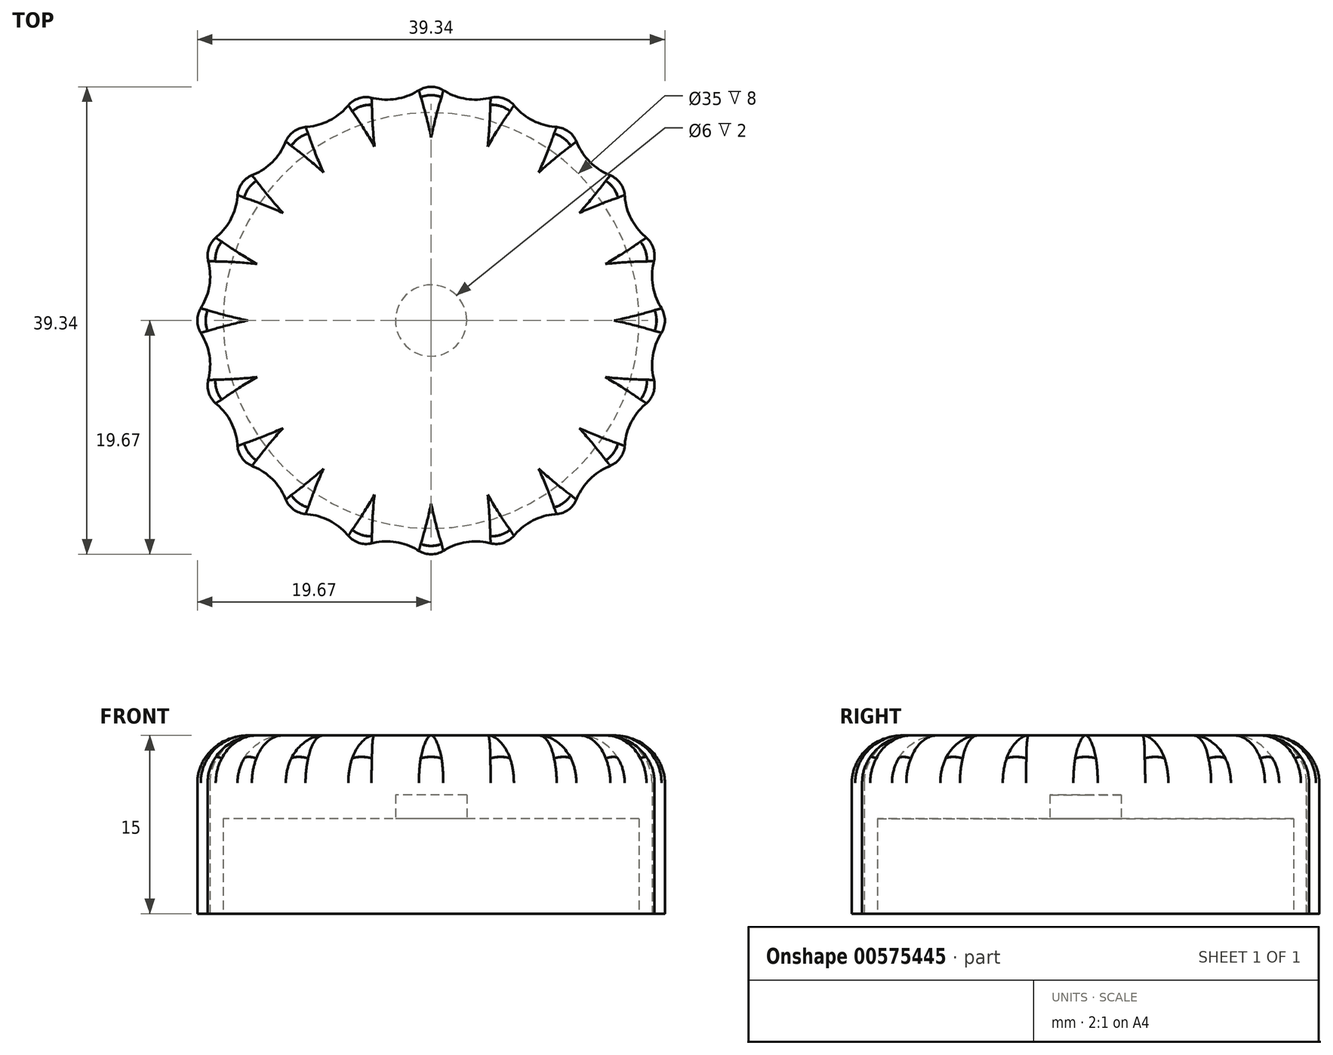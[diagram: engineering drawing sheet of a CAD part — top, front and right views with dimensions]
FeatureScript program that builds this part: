
annotation { "Feature Type Name" : "Feature", "Feature Type Description" : "" }
export const myFeature = defineFeature(function(context is Context, id is Id, definition is map)
    precondition{}
    {
        {
            var Q0;
            Q0=qCreatedBy(makeId("Top.planeOp"),FACE);
            var sketch = newSketch(context, id + "F0", { "sketchPlane" : qUnion([Q0])});
            skCircle(sketch, "E0", {"center": v(0, 0) * mm, "radius": 3 * mm});
            skLineSegment(sketch, "E1", {"start": v(2.6, 1.5) * mm, "end": v(-2.6, 1.5) * mm});
            skCircle(sketch, "E2", {"center": v(0, 0) * mm, "radius": 20 * mm});
            skCircle(sketch, "E3", {"center": v(0, 0) * mm, "radius": 18.5 * mm});
            skCircle(sketch, "E4.cCircle", {"center": v(0, 0) * mm, "radius": 20 * mm, "construction": true});
            skLineSegment(sketch, "E4.0", {"start": v(-20, 0) * mm, "end": v(-19.02, 6.18) * mm});
            skLineSegment(sketch, "E4.1", {"start": v(-19.02, 6.18) * mm, "end": v(-16.18, 11.76) * mm});
            skLineSegment(sketch, "E4.2", {"start": v(-16.18, 11.76) * mm, "end": v(-11.76, 16.18) * mm});
            skLineSegment(sketch, "E4.3", {"start": v(-11.76, 16.18) * mm, "end": v(-6.18, 19.02) * mm});
            skLineSegment(sketch, "E4.4", {"start": v(-6.18, 19.02) * mm, "end": v(0, 20) * mm});
            skLineSegment(sketch, "E4.5", {"start": v(0, 20) * mm, "end": v(6.18, 19.02) * mm});
            skLineSegment(sketch, "E4.6", {"start": v(6.18, 19.02) * mm, "end": v(11.76, 16.18) * mm});
            skLineSegment(sketch, "E4.7", {"start": v(11.76, 16.18) * mm, "end": v(16.18, 11.76) * mm});
            skLineSegment(sketch, "E4.8", {"start": v(16.18, 11.76) * mm, "end": v(19.02, 6.18) * mm});
            skLineSegment(sketch, "E4.9", {"start": v(19.02, 6.18) * mm, "end": v(20, 0) * mm});
            skLineSegment(sketch, "E4.10", {"start": v(20, 0) * mm, "end": v(19.02, -6.18) * mm});
            skLineSegment(sketch, "E4.11", {"start": v(19.02, -6.18) * mm, "end": v(16.18, -11.76) * mm});
            skLineSegment(sketch, "E4.12", {"start": v(16.18, -11.76) * mm, "end": v(11.76, -16.18) * mm});
            skLineSegment(sketch, "E4.13", {"start": v(11.76, -16.18) * mm, "end": v(6.18, -19.02) * mm});
            skLineSegment(sketch, "E4.14", {"start": v(6.18, -19.02) * mm, "end": v(0, -20) * mm});
            skLineSegment(sketch, "E4.15", {"start": v(0, -20) * mm, "end": v(-6.18, -19.02) * mm});
            skLineSegment(sketch, "E4.16", {"start": v(-6.18, -19.02) * mm, "end": v(-11.76, -16.18) * mm});
            skLineSegment(sketch, "E4.17", {"start": v(-11.76, -16.18) * mm, "end": v(-16.18, -11.76) * mm});
            skLineSegment(sketch, "E4.18", {"start": v(-16.18, -11.76) * mm, "end": v(-19.02, -6.18) * mm});
            skLineSegment(sketch, "E4.19", {"start": v(-19.02, -6.18) * mm, "end": v(-20, 0) * mm});
            skCircle(sketch, "E5.cCircle", {"center": v(0, 0) * mm, "radius": 18.5 * mm, "construction": true});
            skLineSegment(sketch, "E5.0", {"start": v(-18.27, -2.9) * mm, "end": v(-18.27, 2.9) * mm});
            skLineSegment(sketch, "E5.1", {"start": v(-18.27, 2.9) * mm, "end": v(-16.48, 8.4) * mm});
            skLineSegment(sketch, "E5.2", {"start": v(-16.48, 8.4) * mm, "end": v(-13.08, 13.08) * mm});
            skLineSegment(sketch, "E5.3", {"start": v(-13.08, 13.08) * mm, "end": v(-8.4, 16.48) * mm});
            skLineSegment(sketch, "E5.4", {"start": v(-8.4, 16.48) * mm, "end": v(-2.9, 18.27) * mm});
            skLineSegment(sketch, "E5.5", {"start": v(-2.9, 18.27) * mm, "end": v(2.9, 18.27) * mm});
            skLineSegment(sketch, "E5.6", {"start": v(2.9, 18.27) * mm, "end": v(8.4, 16.48) * mm});
            skLineSegment(sketch, "E5.7", {"start": v(8.4, 16.48) * mm, "end": v(13.08, 13.08) * mm});
            skLineSegment(sketch, "E5.8", {"start": v(13.08, 13.08) * mm, "end": v(16.48, 8.4) * mm});
            skLineSegment(sketch, "E5.9", {"start": v(16.48, 8.4) * mm, "end": v(18.27, 2.9) * mm});
            skLineSegment(sketch, "E5.10", {"start": v(18.27, 2.9) * mm, "end": v(18.27, -2.9) * mm});
            skLineSegment(sketch, "E5.11", {"start": v(18.27, -2.9) * mm, "end": v(16.48, -8.4) * mm});
            skLineSegment(sketch, "E5.12", {"start": v(16.48, -8.4) * mm, "end": v(13.08, -13.08) * mm});
            skLineSegment(sketch, "E5.13", {"start": v(13.08, -13.08) * mm, "end": v(8.4, -16.48) * mm});
            skLineSegment(sketch, "E5.14", {"start": v(8.4, -16.48) * mm, "end": v(2.9, -18.27) * mm});
            skLineSegment(sketch, "E5.15", {"start": v(2.9, -18.27) * mm, "end": v(-2.9, -18.27) * mm});
            skLineSegment(sketch, "E5.16", {"start": v(-2.9, -18.27) * mm, "end": v(-8.4, -16.48) * mm});
            skLineSegment(sketch, "E5.17", {"start": v(-8.4, -16.48) * mm, "end": v(-13.08, -13.08) * mm});
            skLineSegment(sketch, "E5.18", {"start": v(-13.08, -13.08) * mm, "end": v(-16.48, -8.4) * mm});
            skLineSegment(sketch, "E5.19", {"start": v(-16.48, -8.4) * mm, "end": v(-18.27, -2.9) * mm});
            skLineSegment(sketch, "E6", {"start": v(-18.27, 2.9) * mm, "end": v(-19.02, 6.18) * mm});
            skLineSegment(sketch, "E7", {"start": v(-16.48, 8.4) * mm, "end": v(-19.02, 6.18) * mm});
            skLineSegment(sketch, "E8", {"start": v(-16.18, 11.76) * mm, "end": v(-16.48, 8.4) * mm});
            skLineSegment(sketch, "E9", {"start": v(-13.08, 13.08) * mm, "end": v(-16.18, 11.76) * mm});
            skLineSegment(sketch, "E10", {"start": v(-13.08, 13.08) * mm, "end": v(-11.76, 16.18) * mm});
            skLineSegment(sketch, "E11", {"start": v(-11.76, 16.18) * mm, "end": v(-8.4, 16.48) * mm});
            skLineSegment(sketch, "E12", {"start": v(-8.4, 16.48) * mm, "end": v(-6.18, 19.02) * mm});
            skLineSegment(sketch, "E13", {"start": v(-6.18, 19.02) * mm, "end": v(-2.9, 18.27) * mm});
            skLineSegment(sketch, "E14", {"start": v(-2.9, 18.27) * mm, "end": v(0, 20) * mm});
            skLineSegment(sketch, "E15", {"start": v(2.9, 18.27) * mm, "end": v(0, 20) * mm});
            skLineSegment(sketch, "E16", {"start": v(2.9, 18.27) * mm, "end": v(6.18, 19.02) * mm});
            skLineSegment(sketch, "E17", {"start": v(8.4, 16.48) * mm, "end": v(6.18, 19.02) * mm});
            skLineSegment(sketch, "E18", {"start": v(8.4, 16.48) * mm, "end": v(11.76, 16.18) * mm});
            skLineSegment(sketch, "E19", {"start": v(11.76, 16.18) * mm, "end": v(13.08, 13.08) * mm});
            skLineSegment(sketch, "E20", {"start": v(16.18, 11.76) * mm, "end": v(13.08, 13.08) * mm});
            skLineSegment(sketch, "E21", {"start": v(16.18, 11.76) * mm, "end": v(16.48, 8.4) * mm});
            skLineSegment(sketch, "E22", {"start": v(19.02, 6.18) * mm, "end": v(16.48, 8.4) * mm});
            skLineSegment(sketch, "E23", {"start": v(18.27, 2.9) * mm, "end": v(20, 0) * mm});
            skLineSegment(sketch, "E24", {"start": v(18.27, 2.9) * mm, "end": v(19.02, 6.18) * mm});
            skLineSegment(sketch, "E25", {"start": v(20, 0) * mm, "end": v(18.27, -2.9) * mm});
            skLineSegment(sketch, "E26", {"start": v(19.02, -6.18) * mm, "end": v(18.27, -2.9) * mm});
            skLineSegment(sketch, "E27", {"start": v(16.48, -8.4) * mm, "end": v(19.02, -6.18) * mm});
            skLineSegment(sketch, "E28", {"start": v(16.18, -11.76) * mm, "end": v(16.48, -8.4) * mm});
            skLineSegment(sketch, "E29", {"start": v(16.18, -11.76) * mm, "end": v(13.08, -13.08) * mm});
            skLineSegment(sketch, "E30", {"start": v(13.08, -13.08) * mm, "end": v(11.76, -16.18) * mm});
            skLineSegment(sketch, "E31", {"start": v(11.76, -16.18) * mm, "end": v(8.4, -16.48) * mm});
            skLineSegment(sketch, "E32", {"start": v(8.4, -16.48) * mm, "end": v(6.18, -19.02) * mm});
            skLineSegment(sketch, "E33", {"start": v(6.18, -19.02) * mm, "end": v(2.9, -18.27) * mm});
            skLineSegment(sketch, "E34", {"start": v(2.9, -18.27) * mm, "end": v(0, -20) * mm});
            skLineSegment(sketch, "E35", {"start": v(0, -20) * mm, "end": v(-2.9, -18.27) * mm});
            skLineSegment(sketch, "E36", {"start": v(-2.9, -18.27) * mm, "end": v(-6.18, -19.02) * mm});
            skLineSegment(sketch, "E37", {"start": v(-8.4, -16.48) * mm, "end": v(-6.18, -19.02) * mm});
            skLineSegment(sketch, "E38", {"start": v(-8.4, -16.48) * mm, "end": v(-11.76, -16.18) * mm});
            skLineSegment(sketch, "E39", {"start": v(-13.08, -13.08) * mm, "end": v(-11.76, -16.18) * mm});
            skLineSegment(sketch, "E40", {"start": v(-16.18, -11.76) * mm, "end": v(-13.08, -13.08) * mm});
            skLineSegment(sketch, "E41", {"start": v(-16.18, -11.76) * mm, "end": v(-16.48, -8.4) * mm});
            skLineSegment(sketch, "E42", {"start": v(-19.02, -6.18) * mm, "end": v(-16.48, -8.4) * mm});
            skLineSegment(sketch, "E43", {"start": v(-19.02, -6.18) * mm, "end": v(-18.27, -2.9) * mm});
            skLineSegment(sketch, "E44", {"start": v(-18.27, -2.9) * mm, "end": v(-20, 0) * mm});
            skLineSegment(sketch, "E45", {"start": v(-20, 0) * mm, "end": v(-18.27, 2.9) * mm});
            skCircle(sketch, "E46", {"center": v(0, 0) * mm, "radius": 17.5 * mm});
            skSolve(sketch);
        }
        {
            var Q0;
            {var subQ0=sQuery(id+"F0.wireOp",EDGE,"E1");Q0=makeQuery(id+"F0.imprint","IMPRINT",FACE,{"disambiguationData":[TD([[makeQuery(id+"F0.imprint","IMPRINT",EDGE,{"derivedFrom":subQ0}),1.0]])]});}
            var Q1;
            {var subQ0=sQuery(id+"F0.wireOp",EDGE,"E1");Q1=makeQuery(id+"F0.imprint","IMPRINT",FACE,{"disambiguationData":[TD([[makeQuery(id+"F0.imprint","IMPRINT",EDGE,{"derivedFrom":subQ0}),-1.0]])]});}
            var Q2;
            {var subQ0=sQuery(id+"F0.wireOp",EDGE,"E5.1");Q2=makeQuery(id+"F0.imprint","IMPRINT",FACE,{"disambiguationData":[TD([[makeQuery(id+"F0.imprint","IMPRINT",EDGE,{"derivedFrom":subQ0}),1.0]])]});}
            var Q3;
            {var subQ0=sQuery(id+"F0.wireOp",EDGE,"E6");Q3=makeQuery(id+"F0.imprint","IMPRINT",FACE,{"disambiguationData":[TD([[makeQuery(id+"F0.imprint","IMPRINT",EDGE,{"derivedFrom":subQ0}),-1.0]])]});}
            var Q4;
            {var subQ3=sQuery(id+"F0.wireOp",EDGE,"E42");Q4=makeQuery(id+"F0.imprint","IMPRINT",FACE,{"disambiguationData":[TD([[makeQuery(id+"F0.imprint","IMPRINT",EDGE,{"derivedFrom":subQ3}),1.0]])]});}
            var Q5;
            {var subQ0=sQuery(id+"F0.wireOp",EDGE,"E44");Q5=makeQuery(id+"F0.imprint","IMPRINT",FACE,{"disambiguationData":[TD([[makeQuery(id+"F0.imprint","IMPRINT",EDGE,{"derivedFrom":subQ0}),-1.0]])]});}
            var Q6;
            Q6=makeQuery(id+"F0.imprint","IMPRINT",FACE,{"disambiguationData":[TD([[makeQuery(id+"F0.imprint","IMPRINT",EDGE,{"derivedFrom":sQuery(id+"F0.wireOp",EDGE,"E5.0")}),-1.0]])]});
            var Q7;
            {var subQ0=sQuery(id+"F0.wireOp",EDGE,"E8");Q7=makeQuery(id+"F0.imprint","IMPRINT",FACE,{"disambiguationData":[TD([[makeQuery(id+"F0.imprint","IMPRINT",EDGE,{"derivedFrom":subQ0}),1.0]])]});}
            var Q8;
            {var subQ0=sQuery(id+"F0.wireOp",EDGE,"E10");Q8=makeQuery(id+"F0.imprint","IMPRINT",FACE,{"disambiguationData":[TD([[makeQuery(id+"F0.imprint","IMPRINT",EDGE,{"derivedFrom":subQ0}),-1.0]])]});}
            var Q9;
            {var subQ0=sQuery(id+"F0.wireOp",EDGE,"E12");Q9=makeQuery(id+"F0.imprint","IMPRINT",FACE,{"disambiguationData":[TD([[makeQuery(id+"F0.imprint","IMPRINT",EDGE,{"derivedFrom":subQ0}),-1.0]])]});}
            var Q10;
            {var subQ0=sQuery(id+"F0.wireOp",EDGE,"E14");Q10=makeQuery(id+"F0.imprint","IMPRINT",FACE,{"disambiguationData":[TD([[makeQuery(id+"F0.imprint","IMPRINT",EDGE,{"derivedFrom":subQ0}),-1.0]])]});}
            var Q11;
            {var subQ0=sQuery(id+"F0.wireOp",EDGE,"E16");Q11=makeQuery(id+"F0.imprint","IMPRINT",FACE,{"disambiguationData":[TD([[makeQuery(id+"F0.imprint","IMPRINT",EDGE,{"derivedFrom":subQ0}),-1.0]])]});}
            var Q12;
            {var subQ0=sQuery(id+"F0.wireOp",EDGE,"E18");Q12=makeQuery(id+"F0.imprint","IMPRINT",FACE,{"disambiguationData":[TD([[makeQuery(id+"F0.imprint","IMPRINT",EDGE,{"derivedFrom":subQ0}),-1.0]])]});}
            var Q13;
            {var subQ0=sQuery(id+"F0.wireOp",EDGE,"E20");Q13=makeQuery(id+"F0.imprint","IMPRINT",FACE,{"disambiguationData":[TD([[makeQuery(id+"F0.imprint","IMPRINT",EDGE,{"derivedFrom":subQ0}),1.0]])]});}
            var Q14;
            {var subQ0=sQuery(id+"F0.wireOp",EDGE,"E22");Q14=makeQuery(id+"F0.imprint","IMPRINT",FACE,{"disambiguationData":[TD([[makeQuery(id+"F0.imprint","IMPRINT",EDGE,{"derivedFrom":subQ0}),1.0]])]});}
            var Q15;
            {var subQ0=sQuery(id+"F0.wireOp",EDGE,"E23");Q15=makeQuery(id+"F0.imprint","IMPRINT",FACE,{"disambiguationData":[TD([[makeQuery(id+"F0.imprint","IMPRINT",EDGE,{"derivedFrom":subQ0}),-1.0]])]});}
            var Q16;
            {var subQ0=sQuery(id+"F0.wireOp",EDGE,"E26");Q16=makeQuery(id+"F0.imprint","IMPRINT",FACE,{"disambiguationData":[TD([[makeQuery(id+"F0.imprint","IMPRINT",EDGE,{"derivedFrom":subQ0}),1.0]])]});}
            var Q17;
            {var subQ0=sQuery(id+"F0.wireOp",EDGE,"E28");Q17=makeQuery(id+"F0.imprint","IMPRINT",FACE,{"disambiguationData":[TD([[makeQuery(id+"F0.imprint","IMPRINT",EDGE,{"derivedFrom":subQ0}),1.0]])]});}
            var Q18;
            {var subQ0=sQuery(id+"F0.wireOp",EDGE,"E30");Q18=makeQuery(id+"F0.imprint","IMPRINT",FACE,{"disambiguationData":[TD([[makeQuery(id+"F0.imprint","IMPRINT",EDGE,{"derivedFrom":subQ0}),-1.0]])]});}
            var Q19;
            {var subQ0=sQuery(id+"F0.wireOp",EDGE,"E32");Q19=makeQuery(id+"F0.imprint","IMPRINT",FACE,{"disambiguationData":[TD([[makeQuery(id+"F0.imprint","IMPRINT",EDGE,{"derivedFrom":subQ0}),-1.0]])]});}
            var Q20;
            {var subQ0=sQuery(id+"F0.wireOp",EDGE,"E34");Q20=makeQuery(id+"F0.imprint","IMPRINT",FACE,{"disambiguationData":[TD([[makeQuery(id+"F0.imprint","IMPRINT",EDGE,{"derivedFrom":subQ0}),-1.0]])]});}
            var Q21;
            {var subQ0=sQuery(id+"F0.wireOp",EDGE,"E36");Q21=makeQuery(id+"F0.imprint","IMPRINT",FACE,{"disambiguationData":[TD([[makeQuery(id+"F0.imprint","IMPRINT",EDGE,{"derivedFrom":subQ0}),-1.0]])]});}
            var Q22;
            {var subQ0=sQuery(id+"F0.wireOp",EDGE,"E40");Q22=makeQuery(id+"F0.imprint","IMPRINT",FACE,{"disambiguationData":[TD([[makeQuery(id+"F0.imprint","IMPRINT",EDGE,{"derivedFrom":subQ0}),1.0]])]});}
            var Q23;
            {var subQ0=sQuery(id+"F0.wireOp",EDGE,"E38");Q23=makeQuery(id+"F0.imprint","IMPRINT",FACE,{"disambiguationData":[TD([[makeQuery(id+"F0.imprint","IMPRINT",EDGE,{"derivedFrom":subQ0}),-1.0]])]});}
            var Q24;
            {var subQ0=sQuery(id+"F0.wireOp",EDGE,"E5.0");Q24=makeQuery(id+"F0.imprint","IMPRINT",FACE,{"disambiguationData":[TD([[makeQuery(id+"F0.imprint","IMPRINT",EDGE,{"derivedFrom":subQ0}),1.0]])]});}
            var Q25;
            {var subQ0=sQuery(id+"F0.wireOp",EDGE,"E5.19");Q25=makeQuery(id+"F0.imprint","IMPRINT",FACE,{"disambiguationData":[TD([[makeQuery(id+"F0.imprint","IMPRINT",EDGE,{"derivedFrom":subQ0}),1.0]])]});}
            var Q26;
            {var subQ0=sQuery(id+"F0.wireOp",EDGE,"E5.18");Q26=makeQuery(id+"F0.imprint","IMPRINT",FACE,{"disambiguationData":[TD([[makeQuery(id+"F0.imprint","IMPRINT",EDGE,{"derivedFrom":subQ0}),1.0]])]});}
            var Q27;
            {var subQ0=sQuery(id+"F0.wireOp",EDGE,"E5.2");Q27=makeQuery(id+"F0.imprint","IMPRINT",FACE,{"disambiguationData":[TD([[makeQuery(id+"F0.imprint","IMPRINT",EDGE,{"derivedFrom":subQ0}),1.0]])]});}
            var Q28;
            {var subQ0=sQuery(id+"F0.wireOp",EDGE,"E5.3");Q28=makeQuery(id+"F0.imprint","IMPRINT",FACE,{"disambiguationData":[TD([[makeQuery(id+"F0.imprint","IMPRINT",EDGE,{"derivedFrom":subQ0}),1.0]])]});}
            var Q29;
            {var subQ0=sQuery(id+"F0.wireOp",EDGE,"E5.4");Q29=makeQuery(id+"F0.imprint","IMPRINT",FACE,{"disambiguationData":[TD([[makeQuery(id+"F0.imprint","IMPRINT",EDGE,{"derivedFrom":subQ0}),1.0]])]});}
            var Q30;
            {var subQ0=sQuery(id+"F0.wireOp",EDGE,"E5.6");Q30=makeQuery(id+"F0.imprint","IMPRINT",FACE,{"disambiguationData":[TD([[makeQuery(id+"F0.imprint","IMPRINT",EDGE,{"derivedFrom":subQ0}),1.0]])]});}
            var Q31;
            {var subQ0=sQuery(id+"F0.wireOp",EDGE,"E5.7");Q31=makeQuery(id+"F0.imprint","IMPRINT",FACE,{"disambiguationData":[TD([[makeQuery(id+"F0.imprint","IMPRINT",EDGE,{"derivedFrom":subQ0}),1.0]])]});}
            var Q32;
            {var subQ0=sQuery(id+"F0.wireOp",EDGE,"E5.8");Q32=makeQuery(id+"F0.imprint","IMPRINT",FACE,{"disambiguationData":[TD([[makeQuery(id+"F0.imprint","IMPRINT",EDGE,{"derivedFrom":subQ0}),1.0]])]});}
            var Q33;
            {var subQ0=sQuery(id+"F0.wireOp",EDGE,"E5.9");Q33=makeQuery(id+"F0.imprint","IMPRINT",FACE,{"disambiguationData":[TD([[makeQuery(id+"F0.imprint","IMPRINT",EDGE,{"derivedFrom":subQ0}),1.0]])]});}
            var Q34;
            {var subQ0=sQuery(id+"F0.wireOp",EDGE,"E5.10");Q34=makeQuery(id+"F0.imprint","IMPRINT",FACE,{"disambiguationData":[TD([[makeQuery(id+"F0.imprint","IMPRINT",EDGE,{"derivedFrom":subQ0}),1.0]])]});}
            var Q35;
            {var subQ0=sQuery(id+"F0.wireOp",EDGE,"E5.15");Q35=makeQuery(id+"F0.imprint","IMPRINT",FACE,{"disambiguationData":[TD([[makeQuery(id+"F0.imprint","IMPRINT",EDGE,{"derivedFrom":subQ0}),1.0]])]});}
            var Q36;
            {var subQ0=sQuery(id+"F0.wireOp",EDGE,"E5.14");Q36=makeQuery(id+"F0.imprint","IMPRINT",FACE,{"disambiguationData":[TD([[makeQuery(id+"F0.imprint","IMPRINT",EDGE,{"derivedFrom":subQ0}),1.0]])]});}
            var Q37;
            {var subQ0=sQuery(id+"F0.wireOp",EDGE,"E5.13");Q37=makeQuery(id+"F0.imprint","IMPRINT",FACE,{"disambiguationData":[TD([[makeQuery(id+"F0.imprint","IMPRINT",EDGE,{"derivedFrom":subQ0}),1.0]])]});}
            var Q38;
            {var subQ0=sQuery(id+"F0.wireOp",EDGE,"E5.16");Q38=makeQuery(id+"F0.imprint","IMPRINT",FACE,{"disambiguationData":[TD([[makeQuery(id+"F0.imprint","IMPRINT",EDGE,{"derivedFrom":subQ0}),1.0]])]});}
            var Q39;
            {var subQ0=sQuery(id+"F0.wireOp",EDGE,"E5.5");Q39=makeQuery(id+"F0.imprint","IMPRINT",FACE,{"disambiguationData":[TD([[makeQuery(id+"F0.imprint","IMPRINT",EDGE,{"derivedFrom":subQ0}),1.0]])]});}
            var Q40;
            {var subQ0=sQuery(id+"F0.wireOp",EDGE,"E5.17");Q40=makeQuery(id+"F0.imprint","IMPRINT",FACE,{"disambiguationData":[TD([[makeQuery(id+"F0.imprint","IMPRINT",EDGE,{"derivedFrom":subQ0}),1.0]])]});}
            var Q41;
            {var subQ0=sQuery(id+"F0.wireOp",EDGE,"E5.11");Q41=makeQuery(id+"F0.imprint","IMPRINT",FACE,{"disambiguationData":[TD([[makeQuery(id+"F0.imprint","IMPRINT",EDGE,{"derivedFrom":subQ0}),1.0]])]});}
            var Q42;
            {var subQ0=sQuery(id+"F0.wireOp",EDGE,"E5.12");Q42=makeQuery(id+"F0.imprint","IMPRINT",FACE,{"disambiguationData":[TD([[makeQuery(id+"F0.imprint","IMPRINT",EDGE,{"derivedFrom":subQ0}),1.0]])]});}
            var Q43;
            Q43=makeQuery(id+"F0.imprint","IMPRINT",FACE,{"disambiguationData":[TD([[makeQuery(id+"F0.imprint","IMPRINT",EDGE,{"derivedFrom":sQuery(id+"F0.wireOp",EDGE,"E46")}),1.0]])]});
            extrude(context, id + "F1", {"entities" : qUnion([Q0, Q1, Q2, Q3, Q4, Q5, Q6, Q7, Q8, Q9, Q10, Q11, Q12, Q13, Q14, Q15, Q16, Q17, Q18, Q19, Q20, Q21, Q22, Q23, Q24, Q25, Q26, Q27, Q28, Q29, Q30, Q31, Q32, Q33, Q34, Q35, Q36, Q37, Q38, Q39, Q40, Q41, Q42, Q43]), "depth" : 15 * mm, "offsetDistance" : 25 * mm});
        }
        {
            var Q0;
            {var subQ0=sQuery(id+"F0.wireOp",EDGE,"E1");Q0=makeQuery(id+"F0.imprint","IMPRINT",FACE,{"disambiguationData":[TD([[makeQuery(id+"F0.imprint","IMPRINT",EDGE,{"derivedFrom":subQ0}),1.0]])]});}
            var Q1;
            {var subQ0=sQuery(id+"F0.wireOp",EDGE,"E1");Q1=makeQuery(id+"F0.imprint","IMPRINT",FACE,{"disambiguationData":[TD([[makeQuery(id+"F0.imprint","IMPRINT",EDGE,{"derivedFrom":subQ0}),-1.0]])]});}
            extrude(context, id + "F2", {"entities" : qUnion([Q0, Q1]), "operationType" : NewBodyOperationType.REMOVE, "depth" : 10 * mm, "offsetDistance" : 25 * mm});
        }
        {
            var Q0;
            Q0=makeQuery(id+"F0.imprint","IMPRINT",FACE,{"disambiguationData":[TD([[makeQuery(id+"F0.imprint","IMPRINT",EDGE,{"derivedFrom":sQuery(id+"F0.wireOp",EDGE,"E46")}),1.0]])]});
            extrude(context, id + "F3", {"entities" : qUnion([Q0]), "operationType" : NewBodyOperationType.REMOVE, "depth" : 8 * mm, "offsetDistance" : 25 * mm});
        }
        {
            var Q0;
            Q0=makeQuery(id+"F1.opExtrude","SWEPT_EDGE",EDGE,{"disambiguationData":[OSD([sQuery(id+"F0.wireOp",EDGE,"E2"),sQuery(id+"F0.wireOp",EDGE,"E4.9"),sQuery(id+"F0.wireOp",EDGE,"E4.10"),sQuery(id+"F0.wireOp",EDGE,"E23"),sQuery(id+"F0.wireOp",EDGE,"E25")])]});
            var Q1;
            Q1=makeQuery(id+"F1.opExtrude","SWEPT_EDGE",EDGE,{"disambiguationData":[OSD([sQuery(id+"F0.wireOp",EDGE,"E2"),sQuery(id+"F0.wireOp",EDGE,"E4.10"),sQuery(id+"F0.wireOp",EDGE,"E4.11"),sQuery(id+"F0.wireOp",EDGE,"E26"),sQuery(id+"F0.wireOp",EDGE,"E27")])]});
            var Q2;
            Q2=makeQuery(id+"F1.opExtrude","SWEPT_EDGE",EDGE,{"disambiguationData":[OSD([sQuery(id+"F0.wireOp",EDGE,"E2"),sQuery(id+"F0.wireOp",EDGE,"E4.11"),sQuery(id+"F0.wireOp",EDGE,"E4.12"),sQuery(id+"F0.wireOp",EDGE,"E28"),sQuery(id+"F0.wireOp",EDGE,"E29")])]});
            var Q3;
            Q3=makeQuery(id+"F1.opExtrude","SWEPT_EDGE",EDGE,{"disambiguationData":[OSD([sQuery(id+"F0.wireOp",EDGE,"E2"),sQuery(id+"F0.wireOp",EDGE,"E4.12"),sQuery(id+"F0.wireOp",EDGE,"E4.13"),sQuery(id+"F0.wireOp",EDGE,"E30"),sQuery(id+"F0.wireOp",EDGE,"E31")])]});
            var Q4;
            Q4=makeQuery(id+"F1.opExtrude","SWEPT_EDGE",EDGE,{"disambiguationData":[OSD([sQuery(id+"F0.wireOp",EDGE,"E2"),sQuery(id+"F0.wireOp",EDGE,"E4.13"),sQuery(id+"F0.wireOp",EDGE,"E4.14"),sQuery(id+"F0.wireOp",EDGE,"E32"),sQuery(id+"F0.wireOp",EDGE,"E33")])]});
            var Q5;
            Q5=makeQuery(id+"F1.opExtrude","SWEPT_EDGE",EDGE,{"disambiguationData":[OSD([sQuery(id+"F0.wireOp",EDGE,"E2"),sQuery(id+"F0.wireOp",EDGE,"E4.14"),sQuery(id+"F0.wireOp",EDGE,"E4.15"),sQuery(id+"F0.wireOp",EDGE,"E34"),sQuery(id+"F0.wireOp",EDGE,"E35")])]});
            var Q6;
            Q6=makeQuery(id+"F1.opExtrude","SWEPT_EDGE",EDGE,{"disambiguationData":[OSD([sQuery(id+"F0.wireOp",EDGE,"E2"),sQuery(id+"F0.wireOp",EDGE,"E4.15"),sQuery(id+"F0.wireOp",EDGE,"E4.16"),sQuery(id+"F0.wireOp",EDGE,"E36"),sQuery(id+"F0.wireOp",EDGE,"E37")])]});
            var Q7;
            Q7=makeQuery(id+"F1.opExtrude","SWEPT_EDGE",EDGE,{"disambiguationData":[OSD([sQuery(id+"F0.wireOp",EDGE,"E2"),sQuery(id+"F0.wireOp",EDGE,"E4.16"),sQuery(id+"F0.wireOp",EDGE,"E4.17"),sQuery(id+"F0.wireOp",EDGE,"E38"),sQuery(id+"F0.wireOp",EDGE,"E39")])]});
            var Q8;
            Q8=makeQuery(id+"F1.opExtrude","SWEPT_EDGE",EDGE,{"disambiguationData":[OSD([sQuery(id+"F0.wireOp",EDGE,"E2"),sQuery(id+"F0.wireOp",EDGE,"E4.17"),sQuery(id+"F0.wireOp",EDGE,"E4.18"),sQuery(id+"F0.wireOp",EDGE,"E40"),sQuery(id+"F0.wireOp",EDGE,"E41")])]});
            var Q9;
            Q9=makeQuery(id+"F1.opExtrude","SWEPT_EDGE",EDGE,{"disambiguationData":[OSD([sQuery(id+"F0.wireOp",EDGE,"E2"),sQuery(id+"F0.wireOp",EDGE,"E4.18"),sQuery(id+"F0.wireOp",EDGE,"E4.19"),sQuery(id+"F0.wireOp",EDGE,"E42"),sQuery(id+"F0.wireOp",EDGE,"E43")])]});
            var Q10;
            Q10=makeQuery(id+"F1.opExtrude","SWEPT_EDGE",EDGE,{"disambiguationData":[OSD([sQuery(id+"F0.wireOp",EDGE,"E2"),sQuery(id+"F0.wireOp",EDGE,"E4.0"),sQuery(id+"F0.wireOp",EDGE,"E4.19"),sQuery(id+"F0.wireOp",EDGE,"E44"),sQuery(id+"F0.wireOp",EDGE,"E45")])]});
            var Q11;
            Q11=makeQuery(id+"F1.opExtrude","SWEPT_EDGE",EDGE,{"disambiguationData":[OSD([sQuery(id+"F0.wireOp",EDGE,"E2"),sQuery(id+"F0.wireOp",EDGE,"E4.0"),sQuery(id+"F0.wireOp",EDGE,"E4.1"),sQuery(id+"F0.wireOp",EDGE,"E6"),sQuery(id+"F0.wireOp",EDGE,"E7")])]});
            var Q12;
            Q12=makeQuery(id+"F1.opExtrude","SWEPT_EDGE",EDGE,{"disambiguationData":[OSD([sQuery(id+"F0.wireOp",EDGE,"E2"),sQuery(id+"F0.wireOp",EDGE,"E4.1"),sQuery(id+"F0.wireOp",EDGE,"E4.2"),sQuery(id+"F0.wireOp",EDGE,"E8"),sQuery(id+"F0.wireOp",EDGE,"E9")])]});
            var Q13;
            Q13=makeQuery(id+"F1.opExtrude","SWEPT_EDGE",EDGE,{"disambiguationData":[OSD([sQuery(id+"F0.wireOp",EDGE,"E2"),sQuery(id+"F0.wireOp",EDGE,"E4.2"),sQuery(id+"F0.wireOp",EDGE,"E4.3"),sQuery(id+"F0.wireOp",EDGE,"E10"),sQuery(id+"F0.wireOp",EDGE,"E11")])]});
            var Q14;
            Q14=makeQuery(id+"F1.opExtrude","SWEPT_EDGE",EDGE,{"disambiguationData":[OSD([sQuery(id+"F0.wireOp",EDGE,"E2"),sQuery(id+"F0.wireOp",EDGE,"E4.3"),sQuery(id+"F0.wireOp",EDGE,"E4.4"),sQuery(id+"F0.wireOp",EDGE,"E12"),sQuery(id+"F0.wireOp",EDGE,"E13")])]});
            var Q15;
            Q15=makeQuery(id+"F1.opExtrude","SWEPT_EDGE",EDGE,{"disambiguationData":[OSD([sQuery(id+"F0.wireOp",EDGE,"E2"),sQuery(id+"F0.wireOp",EDGE,"E4.8"),sQuery(id+"F0.wireOp",EDGE,"E4.9"),sQuery(id+"F0.wireOp",EDGE,"E22"),sQuery(id+"F0.wireOp",EDGE,"E24")])]});
            var Q16;
            Q16=makeQuery(id+"F1.opExtrude","SWEPT_EDGE",EDGE,{"disambiguationData":[OSD([sQuery(id+"F0.wireOp",EDGE,"E2"),sQuery(id+"F0.wireOp",EDGE,"E4.7"),sQuery(id+"F0.wireOp",EDGE,"E4.8"),sQuery(id+"F0.wireOp",EDGE,"E20"),sQuery(id+"F0.wireOp",EDGE,"E21")])]});
            var Q17;
            Q17=makeQuery(id+"F1.opExtrude","SWEPT_EDGE",EDGE,{"disambiguationData":[OSD([sQuery(id+"F0.wireOp",EDGE,"E2"),sQuery(id+"F0.wireOp",EDGE,"E4.6"),sQuery(id+"F0.wireOp",EDGE,"E4.7"),sQuery(id+"F0.wireOp",EDGE,"E18"),sQuery(id+"F0.wireOp",EDGE,"E19")])]});
            var Q18;
            Q18=makeQuery(id+"F1.opExtrude","SWEPT_EDGE",EDGE,{"disambiguationData":[OSD([sQuery(id+"F0.wireOp",EDGE,"E2"),sQuery(id+"F0.wireOp",EDGE,"E4.5"),sQuery(id+"F0.wireOp",EDGE,"E4.6"),sQuery(id+"F0.wireOp",EDGE,"E16"),sQuery(id+"F0.wireOp",EDGE,"E17")])]});
            var Q19;
            Q19=makeQuery(id+"F1.opExtrude","SWEPT_EDGE",EDGE,{"disambiguationData":[OSD([sQuery(id+"F0.wireOp",EDGE,"E2"),sQuery(id+"F0.wireOp",EDGE,"E4.4"),sQuery(id+"F0.wireOp",EDGE,"E4.5"),sQuery(id+"F0.wireOp",EDGE,"E14"),sQuery(id+"F0.wireOp",EDGE,"E15")])]});
            fillet(context, id + "F4", {"entities" : qUnion([Q0, Q1, Q2, Q3, Q4, Q5, Q6, Q7, Q8, Q9, Q10, Q11, Q12, Q13, Q14, Q15, Q16, Q17, Q18, Q19]), "radius" : 2 * mm, "tangentPropagation" : true, "allowEdgeOverflow" : false});
        }
        {
            var Q0;
            Q0=makeQuery(id+"F1.opExtrude","SWEPT_EDGE",EDGE,{"disambiguationData":[OSD([sQuery(id+"F0.wireOp",EDGE,"E3"),sQuery(id+"F0.wireOp",EDGE,"E5.2"),sQuery(id+"F0.wireOp",EDGE,"E5.3"),sQuery(id+"F0.wireOp",EDGE,"E9"),sQuery(id+"F0.wireOp",EDGE,"E10")])]});
            var Q1;
            Q1=makeQuery(id+"F1.opExtrude","SWEPT_EDGE",EDGE,{"disambiguationData":[OSD([sQuery(id+"F0.wireOp",EDGE,"E3"),sQuery(id+"F0.wireOp",EDGE,"E5.3"),sQuery(id+"F0.wireOp",EDGE,"E5.4"),sQuery(id+"F0.wireOp",EDGE,"E11"),sQuery(id+"F0.wireOp",EDGE,"E12")])]});
            var Q2;
            Q2=makeQuery(id+"F1.opExtrude","SWEPT_EDGE",EDGE,{"disambiguationData":[OSD([sQuery(id+"F0.wireOp",EDGE,"E3"),sQuery(id+"F0.wireOp",EDGE,"E5.4"),sQuery(id+"F0.wireOp",EDGE,"E5.5"),sQuery(id+"F0.wireOp",EDGE,"E13"),sQuery(id+"F0.wireOp",EDGE,"E14")])]});
            var Q3;
            Q3=makeQuery(id+"F1.opExtrude","SWEPT_EDGE",EDGE,{"disambiguationData":[OSD([sQuery(id+"F0.wireOp",EDGE,"E3"),sQuery(id+"F0.wireOp",EDGE,"E5.5"),sQuery(id+"F0.wireOp",EDGE,"E5.6"),sQuery(id+"F0.wireOp",EDGE,"E15"),sQuery(id+"F0.wireOp",EDGE,"E16")])]});
            var Q4;
            Q4=makeQuery(id+"F1.opExtrude","SWEPT_EDGE",EDGE,{"disambiguationData":[OSD([sQuery(id+"F0.wireOp",EDGE,"E3"),sQuery(id+"F0.wireOp",EDGE,"E5.6"),sQuery(id+"F0.wireOp",EDGE,"E5.7"),sQuery(id+"F0.wireOp",EDGE,"E17"),sQuery(id+"F0.wireOp",EDGE,"E18")])]});
            var Q5;
            Q5=makeQuery(id+"F1.opExtrude","SWEPT_EDGE",EDGE,{"disambiguationData":[OSD([sQuery(id+"F0.wireOp",EDGE,"E3"),sQuery(id+"F0.wireOp",EDGE,"E5.7"),sQuery(id+"F0.wireOp",EDGE,"E5.8"),sQuery(id+"F0.wireOp",EDGE,"E19"),sQuery(id+"F0.wireOp",EDGE,"E20")])]});
            var Q6;
            Q6=makeQuery(id+"F1.opExtrude","SWEPT_EDGE",EDGE,{"disambiguationData":[OSD([sQuery(id+"F0.wireOp",EDGE,"E3"),sQuery(id+"F0.wireOp",EDGE,"E5.8"),sQuery(id+"F0.wireOp",EDGE,"E5.9"),sQuery(id+"F0.wireOp",EDGE,"E21"),sQuery(id+"F0.wireOp",EDGE,"E22")])]});
            var Q7;
            Q7=makeQuery(id+"F1.opExtrude","SWEPT_EDGE",EDGE,{"disambiguationData":[OSD([sQuery(id+"F0.wireOp",EDGE,"E3"),sQuery(id+"F0.wireOp",EDGE,"E5.9"),sQuery(id+"F0.wireOp",EDGE,"E5.10"),sQuery(id+"F0.wireOp",EDGE,"E23"),sQuery(id+"F0.wireOp",EDGE,"E24")])]});
            var Q8;
            Q8=makeQuery(id+"F1.opExtrude","SWEPT_EDGE",EDGE,{"disambiguationData":[OSD([sQuery(id+"F0.wireOp",EDGE,"E3"),sQuery(id+"F0.wireOp",EDGE,"E5.10"),sQuery(id+"F0.wireOp",EDGE,"E5.11"),sQuery(id+"F0.wireOp",EDGE,"E25"),sQuery(id+"F0.wireOp",EDGE,"E26")])]});
            var Q9;
            Q9=makeQuery(id+"F1.opExtrude","SWEPT_EDGE",EDGE,{"disambiguationData":[OSD([sQuery(id+"F0.wireOp",EDGE,"E3"),sQuery(id+"F0.wireOp",EDGE,"E5.11"),sQuery(id+"F0.wireOp",EDGE,"E5.12"),sQuery(id+"F0.wireOp",EDGE,"E27"),sQuery(id+"F0.wireOp",EDGE,"E28")])]});
            var Q10;
            Q10=makeQuery(id+"F1.opExtrude","SWEPT_EDGE",EDGE,{"disambiguationData":[OSD([sQuery(id+"F0.wireOp",EDGE,"E3"),sQuery(id+"F0.wireOp",EDGE,"E5.12"),sQuery(id+"F0.wireOp",EDGE,"E5.13"),sQuery(id+"F0.wireOp",EDGE,"E29"),sQuery(id+"F0.wireOp",EDGE,"E30")])]});
            var Q11;
            Q11=makeQuery(id+"F1.opExtrude","SWEPT_EDGE",EDGE,{"disambiguationData":[OSD([sQuery(id+"F0.wireOp",EDGE,"E3"),sQuery(id+"F0.wireOp",EDGE,"E5.13"),sQuery(id+"F0.wireOp",EDGE,"E5.14"),sQuery(id+"F0.wireOp",EDGE,"E31"),sQuery(id+"F0.wireOp",EDGE,"E32")])]});
            var Q12;
            {var subQ0=sQuery(id+"F0.wireOp",EDGE,"E33");Q12=makeQuery(id+"F4.opFillet","BLEND_EDGE",EDGE,{"blendedFrom":[makeQuery(id+"F1.opExtrude","SWEPT_EDGE",EDGE,{"disambiguationData":[OSD([sQuery(id+"F0.wireOp",EDGE,"E2"),sQuery(id+"F0.wireOp",EDGE,"E4.13"),sQuery(id+"F0.wireOp",EDGE,"E4.14"),sQuery(id+"F0.wireOp",EDGE,"E32"),subQ0])]}),makeQuery(id+"F1.opExtrude","SWEPT_FACE",FACE,{"disambiguationData":[OSD([subQ0])]})],"blendedInto":[makeQuery(id+"F1.opExtrude","SWEPT_FACE",FACE,{"disambiguationData":[OSD([subQ0])]})]});}
            var Q13;
            Q13=makeQuery(id+"F1.opExtrude","SWEPT_EDGE",EDGE,{"disambiguationData":[OSD([sQuery(id+"F0.wireOp",EDGE,"E3"),sQuery(id+"F0.wireOp",EDGE,"E5.14"),sQuery(id+"F0.wireOp",EDGE,"E5.15"),sQuery(id+"F0.wireOp",EDGE,"E33"),sQuery(id+"F0.wireOp",EDGE,"E34")])]});
            var Q14;
            Q14=makeQuery(id+"F1.opExtrude","SWEPT_EDGE",EDGE,{"disambiguationData":[OSD([sQuery(id+"F0.wireOp",EDGE,"E3"),sQuery(id+"F0.wireOp",EDGE,"E5.15"),sQuery(id+"F0.wireOp",EDGE,"E5.16"),sQuery(id+"F0.wireOp",EDGE,"E35"),sQuery(id+"F0.wireOp",EDGE,"E36")])]});
            var Q15;
            Q15=makeQuery(id+"F1.opExtrude","SWEPT_EDGE",EDGE,{"disambiguationData":[OSD([sQuery(id+"F0.wireOp",EDGE,"E3"),sQuery(id+"F0.wireOp",EDGE,"E5.16"),sQuery(id+"F0.wireOp",EDGE,"E5.17"),sQuery(id+"F0.wireOp",EDGE,"E37"),sQuery(id+"F0.wireOp",EDGE,"E38")])]});
            var Q16;
            Q16=makeQuery(id+"F1.opExtrude","SWEPT_EDGE",EDGE,{"disambiguationData":[OSD([sQuery(id+"F0.wireOp",EDGE,"E3"),sQuery(id+"F0.wireOp",EDGE,"E5.17"),sQuery(id+"F0.wireOp",EDGE,"E5.18"),sQuery(id+"F0.wireOp",EDGE,"E39"),sQuery(id+"F0.wireOp",EDGE,"E40")])]});
            var Q17;
            Q17=makeQuery(id+"F1.opExtrude","SWEPT_EDGE",EDGE,{"disambiguationData":[OSD([sQuery(id+"F0.wireOp",EDGE,"E3"),sQuery(id+"F0.wireOp",EDGE,"E5.18"),sQuery(id+"F0.wireOp",EDGE,"E5.19"),sQuery(id+"F0.wireOp",EDGE,"E41"),sQuery(id+"F0.wireOp",EDGE,"E42")])]});
            var Q18;
            Q18=makeQuery(id+"F1.opExtrude","SWEPT_EDGE",EDGE,{"disambiguationData":[OSD([sQuery(id+"F0.wireOp",EDGE,"E3"),sQuery(id+"F0.wireOp",EDGE,"E5.0"),sQuery(id+"F0.wireOp",EDGE,"E5.19"),sQuery(id+"F0.wireOp",EDGE,"E43"),sQuery(id+"F0.wireOp",EDGE,"E44")])]});
            var Q19;
            Q19=makeQuery(id+"F1.opExtrude","SWEPT_EDGE",EDGE,{"disambiguationData":[OSD([sQuery(id+"F0.wireOp",EDGE,"E3"),sQuery(id+"F0.wireOp",EDGE,"E5.0"),sQuery(id+"F0.wireOp",EDGE,"E5.1"),sQuery(id+"F0.wireOp",EDGE,"E6"),sQuery(id+"F0.wireOp",EDGE,"E45")])]});
            var Q20;
            Q20=makeQuery(id+"F1.opExtrude","SWEPT_EDGE",EDGE,{"disambiguationData":[OSD([sQuery(id+"F0.wireOp",EDGE,"E3"),sQuery(id+"F0.wireOp",EDGE,"E5.1"),sQuery(id+"F0.wireOp",EDGE,"E5.2"),sQuery(id+"F0.wireOp",EDGE,"E7"),sQuery(id+"F0.wireOp",EDGE,"E8")])]});
            fillet(context, id + "F5", {"entities" : qUnion([Q0, Q1, Q2, Q3, Q4, Q5, Q6, Q7, Q8, Q9, Q10, Q11, Q12, Q13, Q14, Q15, Q16, Q17, Q18, Q19, Q20]), "radius" : 5 * mm, "tangentPropagation" : true, "allowEdgeOverflow" : false});
        }
        {
            var Q0;
            {var subQ0=sQuery(id+"F0.wireOp",EDGE,"E22");var subQ1=sQuery(id+"F0.wireOp",EDGE,"E21");Q0=makeQuery(id+"F5.opFillet","BLEND_EDGE",EDGE,{"blendedFrom":[makeQuery(id+"F1.opExtrude","SWEPT_EDGE",EDGE,{"disambiguationData":[OSD([sQuery(id+"F0.wireOp",EDGE,"E3"),sQuery(id+"F0.wireOp",EDGE,"E5.8"),sQuery(id+"F0.wireOp",EDGE,"E5.9"),subQ1,subQ0])]}),makeQuery(id+"F1.opExtrude","CAP_FACE",FACE,{"disambiguationData":[OSD([sQuery(id+"F0.wireOp",EDGE,"E6"),sQuery(id+"F0.wireOp",EDGE,"E7"),sQuery(id+"F0.wireOp",EDGE,"E8"),sQuery(id+"F0.wireOp",EDGE,"E9"),sQuery(id+"F0.wireOp",EDGE,"E10"),sQuery(id+"F0.wireOp",EDGE,"E11"),sQuery(id+"F0.wireOp",EDGE,"E12"),sQuery(id+"F0.wireOp",EDGE,"E13"),sQuery(id+"F0.wireOp",EDGE,"E14"),sQuery(id+"F0.wireOp",EDGE,"E15"),sQuery(id+"F0.wireOp",EDGE,"E16"),sQuery(id+"F0.wireOp",EDGE,"E17"),sQuery(id+"F0.wireOp",EDGE,"E18"),sQuery(id+"F0.wireOp",EDGE,"E19"),sQuery(id+"F0.wireOp",EDGE,"E20"),subQ1,subQ0,sQuery(id+"F0.wireOp",EDGE,"E23"),sQuery(id+"F0.wireOp",EDGE,"E24"),sQuery(id+"F0.wireOp",EDGE,"E25"),sQuery(id+"F0.wireOp",EDGE,"E26"),sQuery(id+"F0.wireOp",EDGE,"E27"),sQuery(id+"F0.wireOp",EDGE,"E28"),sQuery(id+"F0.wireOp",EDGE,"E29"),sQuery(id+"F0.wireOp",EDGE,"E30"),sQuery(id+"F0.wireOp",EDGE,"E31"),sQuery(id+"F0.wireOp",EDGE,"E32"),sQuery(id+"F0.wireOp",EDGE,"E33"),sQuery(id+"F0.wireOp",EDGE,"E34"),sQuery(id+"F0.wireOp",EDGE,"E35"),sQuery(id+"F0.wireOp",EDGE,"E36"),sQuery(id+"F0.wireOp",EDGE,"E37"),sQuery(id+"F0.wireOp",EDGE,"E38"),sQuery(id+"F0.wireOp",EDGE,"E39"),sQuery(id+"F0.wireOp",EDGE,"E40"),sQuery(id+"F0.wireOp",EDGE,"E41"),sQuery(id+"F0.wireOp",EDGE,"E42"),sQuery(id+"F0.wireOp",EDGE,"E43"),sQuery(id+"F0.wireOp",EDGE,"E44"),sQuery(id+"F0.wireOp",EDGE,"E45")])],"isStart":false})],"blendedInto":[makeQuery(id+"F1.opExtrude","CAP_FACE",FACE,{"disambiguationData":[OSD([sQuery(id+"F0.wireOp",EDGE,"E6"),sQuery(id+"F0.wireOp",EDGE,"E7"),sQuery(id+"F0.wireOp",EDGE,"E8"),sQuery(id+"F0.wireOp",EDGE,"E9"),sQuery(id+"F0.wireOp",EDGE,"E10"),sQuery(id+"F0.wireOp",EDGE,"E11"),sQuery(id+"F0.wireOp",EDGE,"E12"),sQuery(id+"F0.wireOp",EDGE,"E13"),sQuery(id+"F0.wireOp",EDGE,"E14"),sQuery(id+"F0.wireOp",EDGE,"E15"),sQuery(id+"F0.wireOp",EDGE,"E16"),sQuery(id+"F0.wireOp",EDGE,"E17"),sQuery(id+"F0.wireOp",EDGE,"E18"),sQuery(id+"F0.wireOp",EDGE,"E19"),sQuery(id+"F0.wireOp",EDGE,"E20"),subQ1,subQ0,sQuery(id+"F0.wireOp",EDGE,"E23"),sQuery(id+"F0.wireOp",EDGE,"E24"),sQuery(id+"F0.wireOp",EDGE,"E25"),sQuery(id+"F0.wireOp",EDGE,"E26"),sQuery(id+"F0.wireOp",EDGE,"E27"),sQuery(id+"F0.wireOp",EDGE,"E28"),sQuery(id+"F0.wireOp",EDGE,"E29"),sQuery(id+"F0.wireOp",EDGE,"E30"),sQuery(id+"F0.wireOp",EDGE,"E31"),sQuery(id+"F0.wireOp",EDGE,"E32"),sQuery(id+"F0.wireOp",EDGE,"E33"),sQuery(id+"F0.wireOp",EDGE,"E34"),sQuery(id+"F0.wireOp",EDGE,"E35"),sQuery(id+"F0.wireOp",EDGE,"E36"),sQuery(id+"F0.wireOp",EDGE,"E37"),sQuery(id+"F0.wireOp",EDGE,"E38"),sQuery(id+"F0.wireOp",EDGE,"E39"),sQuery(id+"F0.wireOp",EDGE,"E40"),sQuery(id+"F0.wireOp",EDGE,"E41"),sQuery(id+"F0.wireOp",EDGE,"E42"),sQuery(id+"F0.wireOp",EDGE,"E43"),sQuery(id+"F0.wireOp",EDGE,"E44"),sQuery(id+"F0.wireOp",EDGE,"E45")])],"isStart":false})]});}
            fillet(context, id + "F6", {"entities" : qUnion([Q0]), "radius" : 4 * mm, "tangentPropagation" : true, "allowEdgeOverflow" : false});
        }
    });
